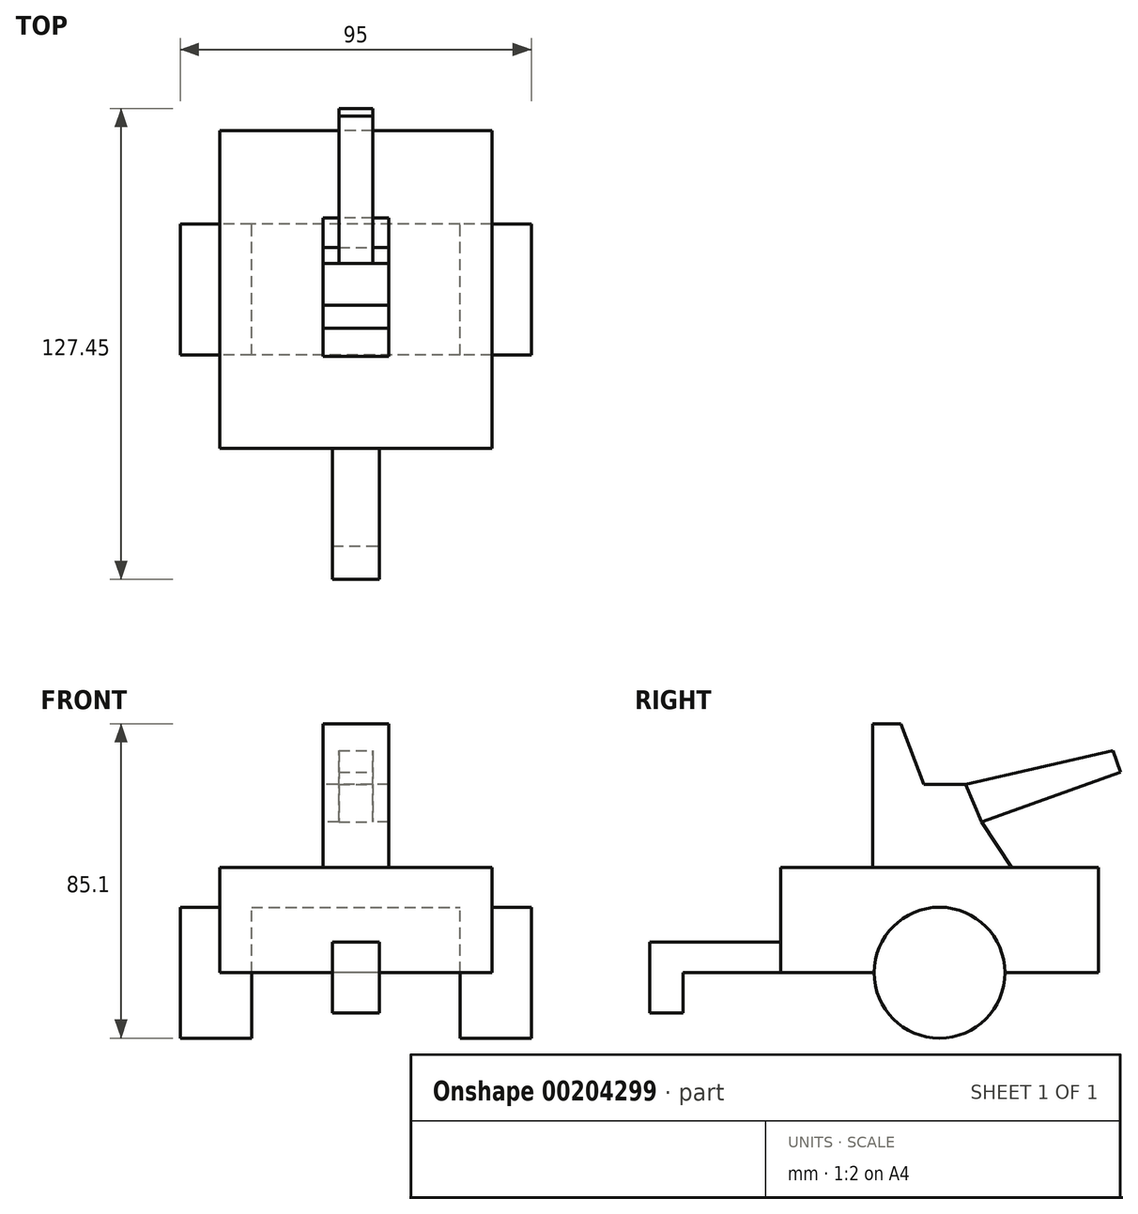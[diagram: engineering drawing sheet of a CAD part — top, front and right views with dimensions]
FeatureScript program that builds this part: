
annotation { "Feature Type Name" : "Feature", "Feature Type Description" : "" }
export const myFeature = defineFeature(function(context is Context, id is Id, definition is map)
    precondition{}
    {
        {
            var Q0;
            Q0=qCreatedBy(makeId("Right.planeOp"),FACE);
            var sketch = newSketch(context, id + "F0", { "sketchPlane" : qUnion([Q0])});
            skLineSegment(sketch, "E0.bottom", {"start": v(-43, 14.22) * mm, "end": v(43, 14.22) * mm});
            skLineSegment(sketch, "E0.top", {"start": v(-43, -14.22) * mm, "end": v(-17.7, -14.22) * mm});
            skLineSegment(sketch, "E0.left", {"start": v(-43, 14.22) * mm, "end": v(-43, -14.22) * mm});
            skLineSegment(sketch, "E0.right", {"start": v(43, 14.22) * mm, "end": v(43, -14.22) * mm});
            skPoint(sketch, "E0.middle", {"position": v(0, 0) * mm});
            skCircle(sketch, "E1", {"center": v(0, -14.22) * mm, "radius": 17.7 * mm});
            skLineSegment(sketch, "E2.trimOffspring", {"start": v(17.7, -14.22) * mm, "end": v(43, -14.22) * mm});
            skLineSegment(sketch, "E3", {"start": v(19.46, 14.22) * mm, "end": v(11.43, 26.54) * mm});
            skLineSegment(sketch, "E4", {"start": v(11.43, 26.54) * mm, "end": v(49.01, 40.04) * mm});
            skLineSegment(sketch, "E5", {"start": v(49.01, 40.04) * mm, "end": v(46.93, 45.84) * mm});
            skLineSegment(sketch, "E6", {"start": v(46.93, 45.84) * mm, "end": v(7.05, 36.76) * mm});
            skLineSegment(sketch, "E7", {"start": v(7.05, 36.76) * mm, "end": v(-4.26, 36.76) * mm});
            skLineSegment(sketch, "E8", {"start": v(-4.26, 36.76) * mm, "end": v(-10.46, 53.17) * mm});
            skLineSegment(sketch, "E9", {"start": v(-10.46, 53.17) * mm, "end": v(-18.12, 53.17) * mm});
            skLineSegment(sketch, "E10", {"start": v(-18.12, 53.17) * mm, "end": v(-18.12, 14.22) * mm});
            skLineSegment(sketch, "E11", {"start": v(-43, -14.22) * mm, "end": v(-78.44, -14.22) * mm});
            skLineSegment(sketch, "E12", {"start": v(-78.44, -14.22) * mm, "end": v(-78.44, -5.93) * mm});
            skLineSegment(sketch, "E13", {"start": v(-78.44, -5.93) * mm, "end": v(-43, -5.93) * mm});
            skLineSegment(sketch, "E14", {"start": v(-78.44, -14.22) * mm, "end": v(-78.44, -31.28) * mm});
            skLineSegment(sketch, "E15", {"start": v(-78.44, -31.28) * mm, "end": v(-69.34, -31.36) * mm});
            skLineSegment(sketch, "E16", {"start": v(-69.34, -31.36) * mm, "end": v(-69.34, -14.22) * mm});
            skLineSegment(sketch, "E17", {"start": v(7.05, 36.76) * mm, "end": v(11.43, 26.54) * mm});
            skSolve(sketch);
        }
        {
            var Q0;
            {var subQ0=sQuery(id+"F0.wireOp",EDGE,"E0.top");Q0=makeQuery(id+"F0.imprint","IMPRINT",FACE,{"disambiguationData":[TD([[makeQuery(id+"F0.imprint","IMPRINT",EDGE,{"derivedFrom":subQ0}),1.0]])]});}
            extrude(context, id + "F1", {"entities" : qUnion([Q0]), "endBound" : BoundingType.SYMMETRIC, "depth" : 73.66 * mm});
        }
        {
            var Q0;
            {var subQ0=sQuery(id+"F0.wireOp",EDGE,"E1");var subQ1=makeQuery(id+"F0.imprint","INTERSECT",VERTEX,{"derivedFrom":[sQuery(id+"F0.wireOp",EDGE,"E0.top"),subQ0]});Q0=makeQuery(id+"F0.imprint","IMPRINT",FACE,{"disambiguationData":[TD([[makeQuery(id+"F0.imprint","IMPRINT",EDGE,{"disambiguationData":[TD([[subQ1,1.0]])],"derivedFrom":subQ0}),1.0]])]});}
            extrude(context, id + "F2", {"entities" : qUnion([Q0]), "operationType" : NewBodyOperationType.ADD, "endBound" : BoundingType.SYMMETRIC, "depth" : 95 * mm});
        }
        {
            var Q0;
            {var subQ0=sQuery(id+"F0.wireOp",EDGE,"E1");var subQ1=makeQuery(id+"F0.imprint","INTERSECT",VERTEX,{"derivedFrom":[sQuery(id+"F0.wireOp",EDGE,"E0.top"),subQ0]});Q0=makeQuery(id+"F0.imprint","IMPRINT",FACE,{"disambiguationData":[TD([[makeQuery(id+"F0.imprint","IMPRINT",EDGE,{"disambiguationData":[TD([[subQ1,1.0]])],"derivedFrom":subQ0}),1.0]])]});}
            extrude(context, id + "F3", {"entities" : qUnion([Q0]), "operationType" : NewBodyOperationType.REMOVE, "endBound" : BoundingType.SYMMETRIC, "oppositeDirection" : true, "depth" : 56.4 * mm});
        }
        {
            var Q0;
            {var subQ0=sQuery(id+"F0.wireOp",EDGE,"E3");Q0=makeQuery(id+"F0.imprint","IMPRINT",FACE,{"disambiguationData":[TD([[makeQuery(id+"F0.imprint","IMPRINT",EDGE,{"derivedFrom":subQ0}),1.0]])]});}
            extrude(context, id + "F4", {"entities" : qUnion([Q0]), "operationType" : NewBodyOperationType.ADD, "endBound" : BoundingType.SYMMETRIC, "depth" : 17.78 * mm});
        }
        {
            var Q0;
            Q0=makeQuery(id+"F0.imprint","IMPRINT",FACE,{"disambiguationData":[TD([[makeQuery(id+"F0.imprint","IMPRINT",EDGE,{"derivedFrom":sQuery(id+"F0.wireOp",EDGE,"E4")}),1.0]])]});
            extrude(context, id + "F5", {"entities" : qUnion([Q0]), "operationType" : NewBodyOperationType.ADD, "endBound" : BoundingType.SYMMETRIC, "oppositeDirection" : true, "depth" : 9.14 * mm});
        }
        {
            var Q0;
            {var subQ4=sQuery(id+"F0.wireOp",EDGE,"E12");Q0=makeQuery(id+"F0.imprint","IMPRINT",FACE,{"disambiguationData":[TD([[makeQuery(id+"F0.imprint","IMPRINT",EDGE,{"derivedFrom":subQ4}),-1.0]])]});}
            var Q1;
            {var subQ0=sQuery(id+"F0.wireOp",EDGE,"E14");Q1=makeQuery(id+"F0.imprint","IMPRINT",FACE,{"disambiguationData":[TD([[makeQuery(id+"F0.imprint","IMPRINT",EDGE,{"derivedFrom":subQ0}),1.0]])]});}
            extrude(context, id + "F6", {"entities" : qUnion([Q0, Q1]), "operationType" : NewBodyOperationType.ADD, "endBound" : BoundingType.SYMMETRIC, "depth" : 12.7 * mm});
        }
        {
            var Q0;
            Q0=qCreatedBy(makeId("Right.planeOp"),FACE);
            var sketch = newSketch(context, id + "F7", { "sketchPlane" : qUnion([Q0])});
            skLineSegment(sketch, "E18.bottom", {"start": v(-88.88, -25.1) * mm, "end": v(-54.92, -25.1) * mm});
            skLineSegment(sketch, "E18.top", {"start": v(-88.88, -36.43) * mm, "end": v(-54.92, -36.43) * mm});
            skLineSegment(sketch, "E18.left", {"start": v(-88.88, -25.1) * mm, "end": v(-88.88, -36.43) * mm});
            skLineSegment(sketch, "E18.right", {"start": v(-54.92, -25.1) * mm, "end": v(-54.92, -36.43) * mm});
            skSolve(sketch);
        }
        {
            var Q0;
            Q0=makeQuery(id+"F7.imprint","IMPRINT",FACE,{"disambiguationData":[TD([[makeQuery(id+"F7.imprint","IMPRINT",EDGE,{"derivedFrom":sQuery(id+"F7.wireOp",EDGE,"E18.bottom")}),-1.0]])]});
            extrude(context, id + "F8", {"entities" : qUnion([Q0]), "operationType" : NewBodyOperationType.REMOVE, "endBound" : BoundingType.SYMMETRIC, "oppositeDirection" : true, "depth" : 25.4 * mm});
        }
    });
